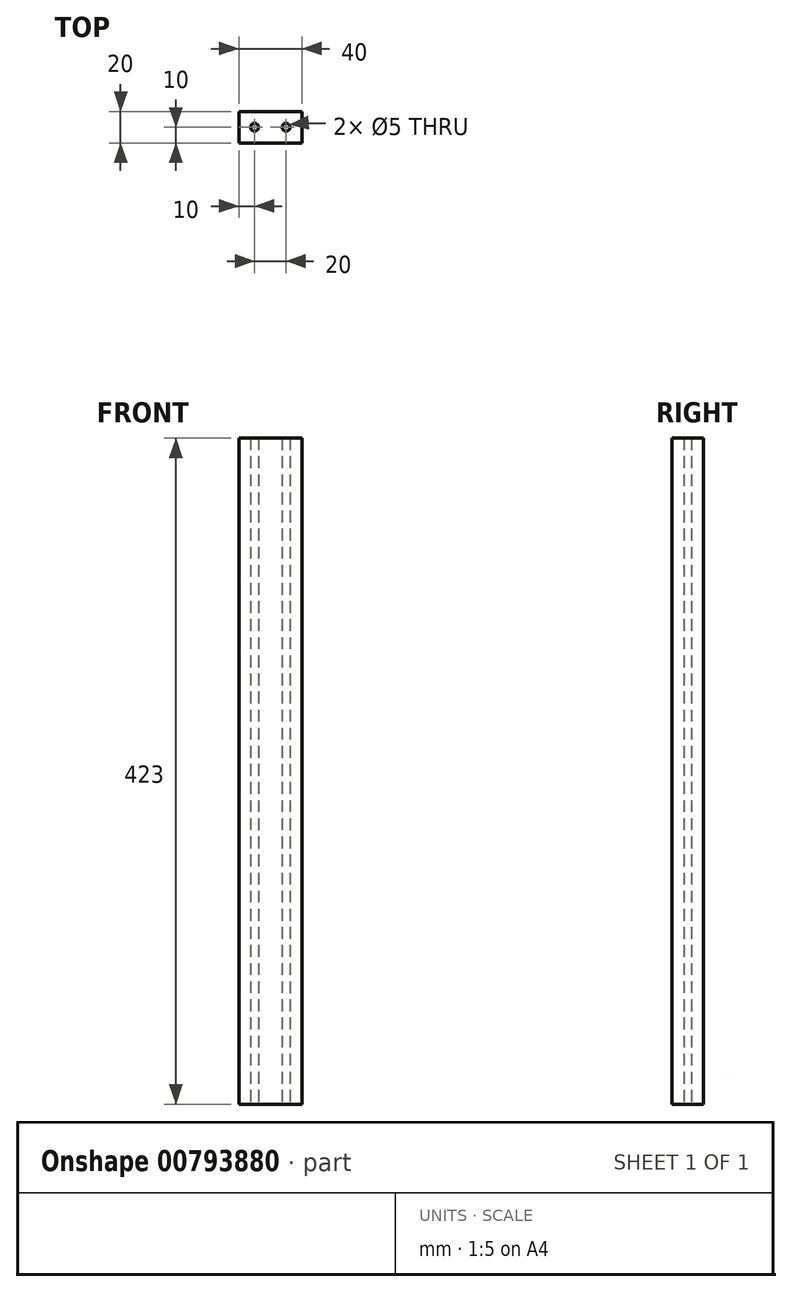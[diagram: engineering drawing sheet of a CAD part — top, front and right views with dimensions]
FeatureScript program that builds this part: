
annotation { "Feature Type Name" : "Feature", "Feature Type Description" : "" }
export const myFeature = defineFeature(function(context is Context, id is Id, definition is map)
    precondition{}
    {
        {
            var Q0;
            Q0=qCreatedBy(makeId("Top.planeOp"),FACE);
            var sketch = newSketch(context, id + "F0", { "sketchPlane" : qUnion([Q0])});
            skLineSegment(sketch, "E0.bottom", {"start": v(-20, 10) * mm, "end": v(20, 10) * mm});
            skLineSegment(sketch, "E0.top", {"start": v(-20, -10) * mm, "end": v(20, -10) * mm});
            skLineSegment(sketch, "E0.left", {"start": v(-20, 10) * mm, "end": v(-20, -10) * mm});
            skLineSegment(sketch, "E0.right", {"start": v(20, 10) * mm, "end": v(20, -10) * mm});
            skCircle(sketch, "E1", {"center": v(-10, 0) * mm, "radius": 2.5 * mm});
            skCircle(sketch, "E2", {"center": v(10, 0) * mm, "radius": 2.5 * mm});
            skSolve(sketch);
        }
        {
            var Q0;
            Q0=qSketchRegion(id+"F0",true);
            extrude(context, id + "F1", {"entities" : qUnion([Q0]), "depth" : 423 * mm, "offsetDistance" : 25 * mm});
        }
        {
            var Q0;
            Q0=makeQuery(id+"F1.opExtrude","SWEPT_FACE",FACE,{"disambiguationData":[OSD([sQuery(id+"F0.wireOp",EDGE,"E0.right")])]});
            var sketch = newSketch(context, id + "F2", { "sketchPlane" : qUnion([Q0])});
            skCircle(sketch, "E3", {"center": v(0, 10) * mm, "radius": 2.5 * mm});
            skSolve(sketch);
        }
        {
            var Q0;
            Q0=makeQuery(id+"F1.opExtrude","SWEPT_FACE",FACE,{"disambiguationData":[OSD([sQuery(id+"F0.wireOp",EDGE,"E0.top")])]});
            var sketch = newSketch(context, id + "F3", { "sketchPlane" : qUnion([Q0])});
            skCircle(sketch, "E4", {"center": v(0, 211.5) * mm, "radius": 2.5 * mm});
            skPoint(sketch, "E4.centerSnap0", {"position": v(-20, 211.5) * mm});
            skSolve(sketch);
        }
        {
            var Q0;
            Q0=makeQuery(id+"F3.imprint","IMPRINT",FACE,{"disambiguationData":[TD([[makeQuery(id+"F3.imprint","IMPRINT",EDGE,{"derivedFrom":sQuery(id+"F3.wireOp",EDGE,"E4")}),-1.0]])]});
            var sketch = newSketch(context, id + "F4", { "sketchPlane" : qUnion([Q0])});
            skCircle(sketch, "E5", {"center": v(10, 10) * mm, "radius": 2.5 * mm});
            skCircle(sketch, "E6", {"center": v(10, 413) * mm, "radius": 2.5 * mm});
            skSolve(sketch);
        }
    });
